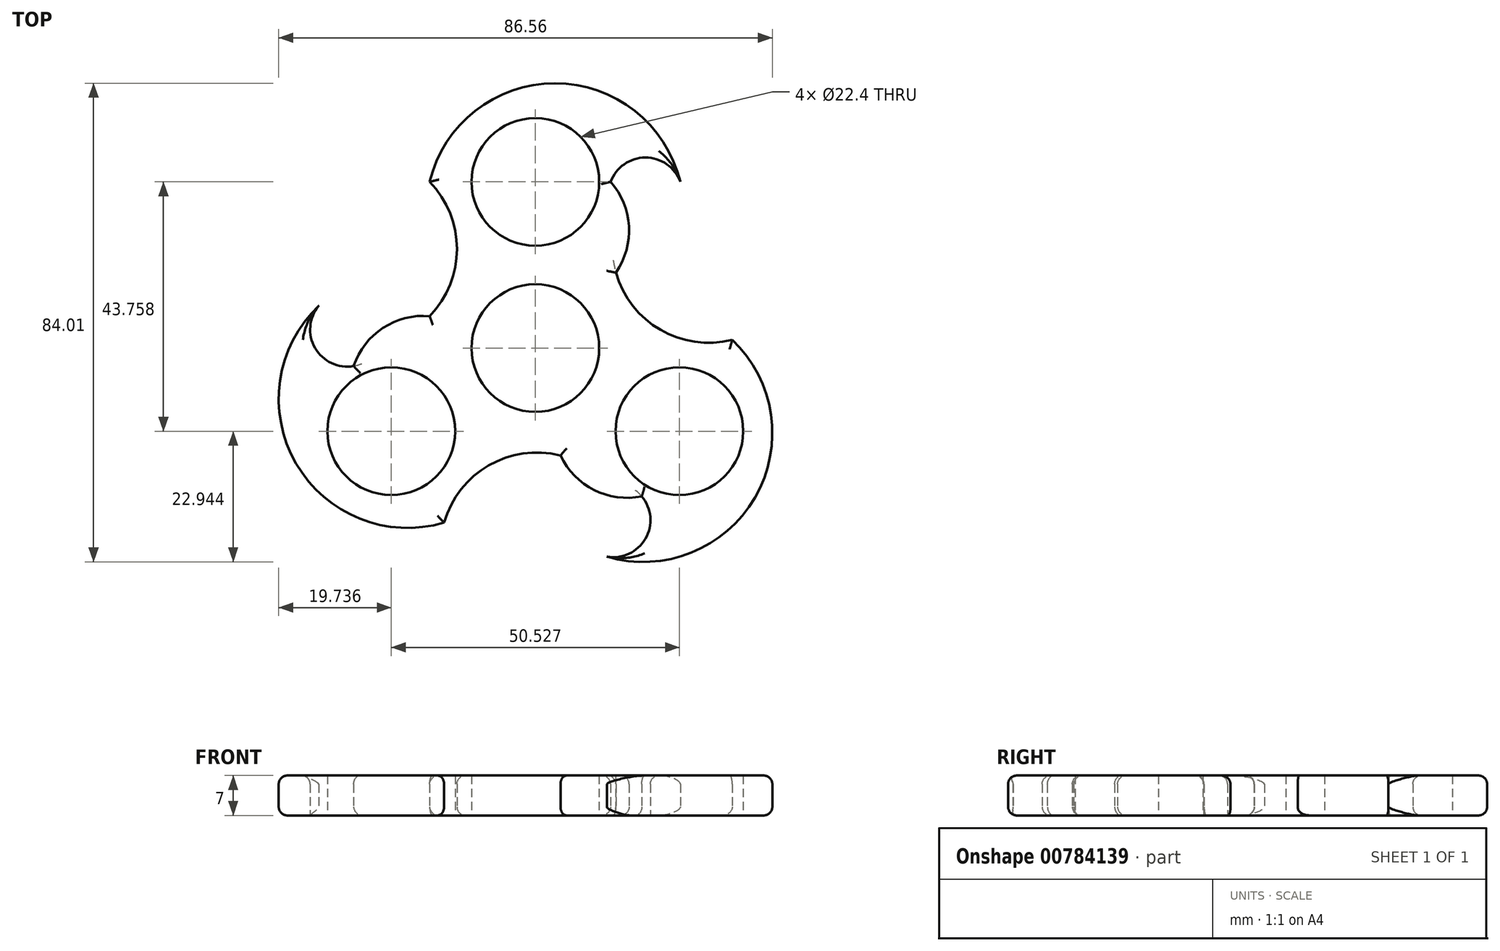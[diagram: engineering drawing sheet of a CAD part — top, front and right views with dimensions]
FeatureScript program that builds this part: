
annotation { "Feature Type Name" : "Feature", "Feature Type Description" : "" }
export const myFeature = defineFeature(function(context is Context, id is Id, definition is map)
    precondition{}
    {
        {
            var Q0;
            Q0=qCreatedBy(makeId("Top.planeOp"),FACE);
            var sketch = newSketch(context, id + "F0", { "sketchPlane" : qUnion([Q0])});
            skCircle(sketch, "E0", {"center": v(0, 0) * mm, "radius": 11.2 * mm});
            skCircle(sketch, "E1", {"center": v(0, 29.17) * mm, "radius": 11.2 * mm});
            skCircle(sketch, "E2.1.1", {"center": v(-25.26, -14.59) * mm, "radius": 11.2 * mm});
            skCircle(sketch, "E2.2.1", {"center": v(25.26, -14.59) * mm, "radius": 11.2 * mm});
            skArc(sketch, "E3", {"start": v(25.44, 29.17) * mm, "mid": v(3.45, 46.48) * mm, "end": v(-18.54, 29.17) * mm});
            skArc(sketch, "E4", {"start": v(25.44, 29.17) * mm, "mid": v(19.32, 33.45) * mm, "end": v(13.2, 29.17) * mm});
            skArc(sketch, "E5", {"start": v(-18.54, 5.6) * mm, "mid": v(-13.75, 17.39) * mm, "end": v(-18.54, 29.17) * mm});
            skArc(sketch, "E6.1.0", {"start": v(-37.98, 7.44) * mm, "mid": v(-41.97, -20.25) * mm, "end": v(-16, -30.64) * mm});
            skArc(sketch, "E6.1.1", {"start": v(4.42, -18.86) * mm, "mid": v(-8.18, -20.6) * mm, "end": v(-16, -30.64) * mm});
            skArc(sketch, "E6.1.2", {"start": v(-37.98, 7.44) * mm, "mid": v(-38.63, 0) * mm, "end": v(-31.86, -3.15) * mm});
            skArc(sketch, "E6.2.0", {"start": v(12.55, -36.61) * mm, "mid": v(38.52, -26.22) * mm, "end": v(34.53, 1.47) * mm});
            skArc(sketch, "E6.2.1", {"start": v(14.12, 13.25) * mm, "mid": v(21.94, 3.22) * mm, "end": v(34.53, 1.47) * mm});
            skArc(sketch, "E6.2.2", {"start": v(12.55, -36.61) * mm, "mid": v(19.3, -33.45) * mm, "end": v(18.66, -26.02) * mm});
            skArc(sketch, "E7", {"start": v(14.12, 13.25) * mm, "mid": v(16.42, 21.37) * mm, "end": v(13.2, 29.17) * mm});
            skArc(sketch, "E8.1.0", {"start": v(-18.54, 5.6) * mm, "mid": v(-26.72, 3.54) * mm, "end": v(-31.86, -3.15) * mm});
            skArc(sketch, "E8.2.0", {"start": v(4.42, -18.86) * mm, "mid": v(10.3, -24.9) * mm, "end": v(18.66, -26.02) * mm});
            skSolve(sketch);
        }
        {
            var Q0;
            Q0=makeQuery(id+"F0.imprint","IMPRINT",FACE,{"disambiguationData":[TD([[makeQuery(id+"F0.imprint","IMPRINT",EDGE,{"derivedFrom":sQuery(id+"F0.wireOp",EDGE,"E0")}),-1.0]])]});
            extrude(context, id + "F1", {"entities" : qUnion([Q0]), "depth" : 7 * mm, "offsetDistance" : 25 * mm});
        }
        {
            var Q0;
            Q0=makeQuery(id+"F1.opExtrude","CAP_EDGE",EDGE,{"disambiguationData":[OSD([sQuery(id+"F0.wireOp",EDGE,"E6.1.1")])],"isStart":false});
            var Q1;
            Q1=makeQuery(id+"F1.opExtrude","CAP_EDGE",EDGE,{"disambiguationData":[OSD([sQuery(id+"F0.wireOp",EDGE,"E8.2.0")])],"isStart":false});
            var Q2;
            Q2=makeQuery(id+"F1.opExtrude","CAP_EDGE",EDGE,{"disambiguationData":[OSD([sQuery(id+"F0.wireOp",EDGE,"E6.2.0")])],"isStart":false});
            var Q3;
            Q3=makeQuery(id+"F1.opExtrude","CAP_EDGE",EDGE,{"disambiguationData":[OSD([sQuery(id+"F0.wireOp",EDGE,"E7")])],"isStart":false});
            var Q4;
            Q4=makeQuery(id+"F1.opExtrude","CAP_EDGE",EDGE,{"disambiguationData":[OSD([sQuery(id+"F0.wireOp",EDGE,"E4")])],"isStart":false});
            var Q5;
            Q5=makeQuery(id+"F1.opExtrude","CAP_EDGE",EDGE,{"disambiguationData":[OSD([sQuery(id+"F0.wireOp",EDGE,"E6.2.1")])],"isStart":false});
            var Q6;
            Q6=makeQuery(id+"F1.opExtrude","CAP_EDGE",EDGE,{"disambiguationData":[OSD([sQuery(id+"F0.wireOp",EDGE,"E7")])],"isStart":true});
            var Q7;
            Q7=makeQuery(id+"F1.opExtrude","CAP_EDGE",EDGE,{"disambiguationData":[OSD([sQuery(id+"F0.wireOp",EDGE,"E4")])],"isStart":true});
            var Q8;
            Q8=makeQuery(id+"F1.opExtrude","CAP_EDGE",EDGE,{"disambiguationData":[OSD([sQuery(id+"F0.wireOp",EDGE,"E3")])],"isStart":false});
            var Q9;
            Q9=makeQuery(id+"F1.opExtrude","CAP_EDGE",EDGE,{"disambiguationData":[OSD([sQuery(id+"F0.wireOp",EDGE,"E5")])],"isStart":false});
            var Q10;
            Q10=makeQuery(id+"F1.opExtrude","CAP_EDGE",EDGE,{"disambiguationData":[OSD([sQuery(id+"F0.wireOp",EDGE,"E8.1.0")])],"isStart":false});
            var Q11;
            Q11=makeQuery(id+"F1.opExtrude","CAP_EDGE",EDGE,{"disambiguationData":[OSD([sQuery(id+"F0.wireOp",EDGE,"E6.1.2")])],"isStart":false});
            var Q12;
            Q12=makeQuery(id+"F1.opExtrude","CAP_EDGE",EDGE,{"disambiguationData":[OSD([sQuery(id+"F0.wireOp",EDGE,"E6.1.0")])],"isStart":false});
            var Q13;
            Q13=makeQuery(id+"F1.opExtrude","CAP_EDGE",EDGE,{"disambiguationData":[OSD([sQuery(id+"F0.wireOp",EDGE,"E6.1.0")])],"isStart":true});
            var Q14;
            Q14=makeQuery(id+"F1.opExtrude","CAP_EDGE",EDGE,{"disambiguationData":[OSD([sQuery(id+"F0.wireOp",EDGE,"E6.1.1")])],"isStart":true});
            var Q15;
            Q15=makeQuery(id+"F1.opExtrude","CAP_EDGE",EDGE,{"disambiguationData":[OSD([sQuery(id+"F0.wireOp",EDGE,"E6.2.2")])],"isStart":false});
            var Q16;
            Q16=makeQuery(id+"F1.opExtrude","CAP_EDGE",EDGE,{"disambiguationData":[OSD([sQuery(id+"F0.wireOp",EDGE,"E6.2.0")])],"isStart":true});
            var Q17;
            Q17=makeQuery(id+"F1.opExtrude","CAP_EDGE",EDGE,{"disambiguationData":[OSD([sQuery(id+"F0.wireOp",EDGE,"E8.2.0")])],"isStart":true});
            var Q18;
            Q18=makeQuery(id+"F1.opExtrude","CAP_EDGE",EDGE,{"disambiguationData":[OSD([sQuery(id+"F0.wireOp",EDGE,"E3")])],"isStart":true});
            var Q19;
            Q19=makeQuery(id+"F1.opExtrude","CAP_EDGE",EDGE,{"disambiguationData":[OSD([sQuery(id+"F0.wireOp",EDGE,"E5")])],"isStart":true});
            var Q20;
            Q20=makeQuery(id+"F1.opExtrude","CAP_EDGE",EDGE,{"disambiguationData":[OSD([sQuery(id+"F0.wireOp",EDGE,"E8.1.0")])],"isStart":true});
            fillet(context, id + "F2", {"entities" : qUnion([Q0, Q1, Q2, Q3, Q4, Q5, Q6, Q7, Q8, Q9, Q10, Q11, Q12, Q13, Q14, Q15, Q16, Q17, Q18, Q19, Q20]), "radius" : 1.5 * mm, "tangentPropagation" : true, "allowEdgeOverflow" : false});
        }
    });
